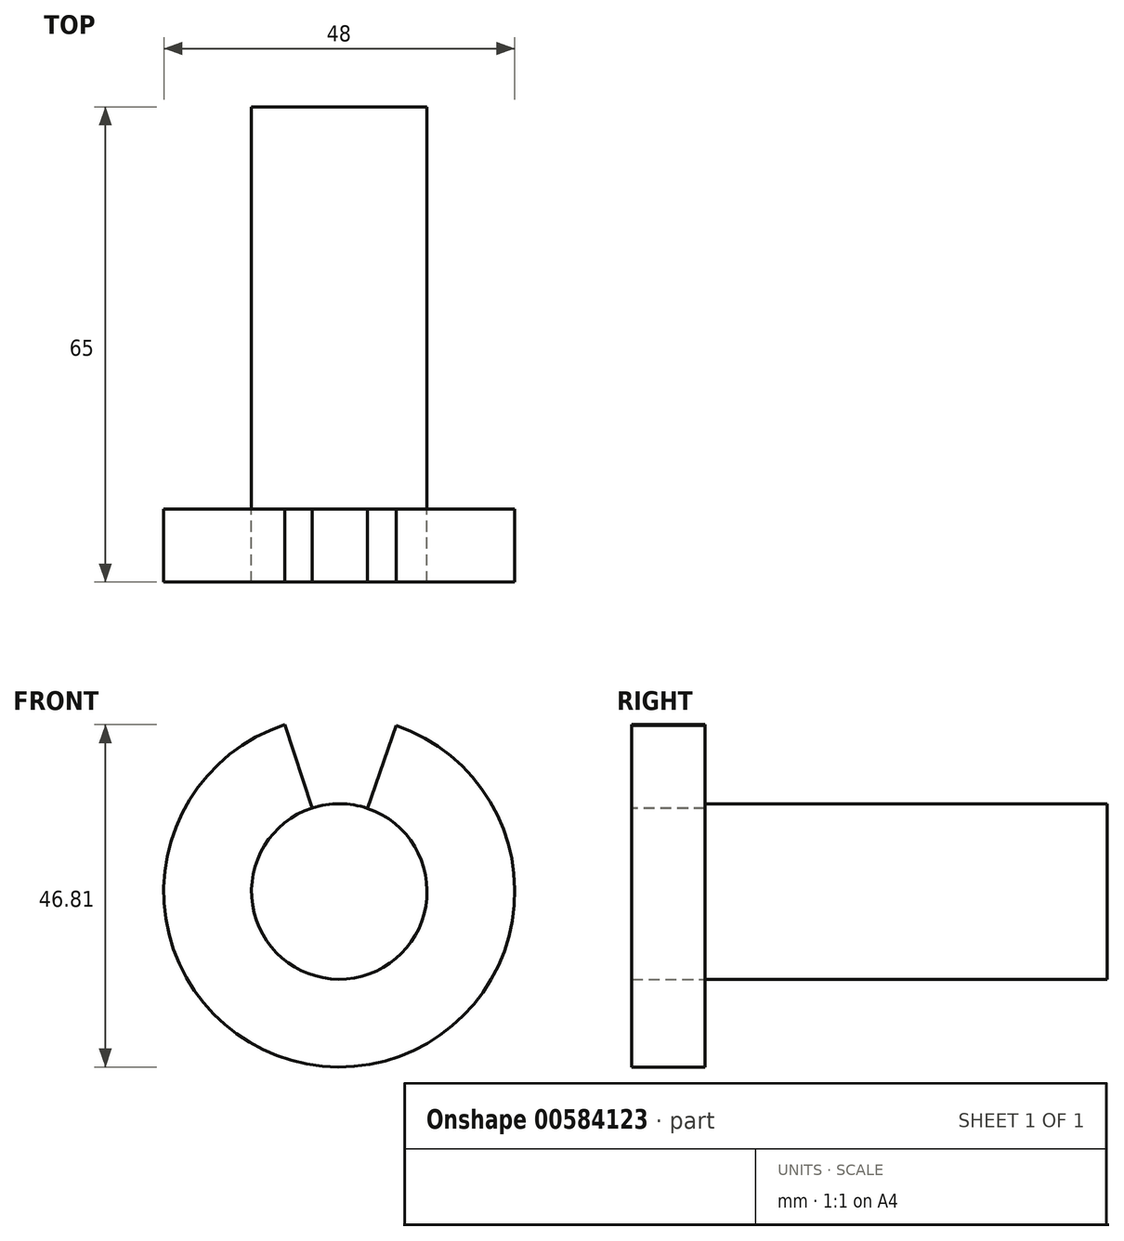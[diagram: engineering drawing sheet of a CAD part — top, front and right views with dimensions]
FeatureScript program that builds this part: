
annotation { "Feature Type Name" : "Feature", "Feature Type Description" : "" }
export const myFeature = defineFeature(function(context is Context, id is Id, definition is map)
    precondition{}
    {
        {
            var Q0;
            Q0=qCreatedBy(makeId("Front.planeOp"),FACE);
            var sketch = newSketch(context, id + "F0", { "sketchPlane" : qUnion([Q0])});
            skCircle(sketch, "E0", {"center": v(-28.82, 43.35) * mm, "radius": 12 * mm});
            skSolve(sketch);
        }
        {
            var Q0;
            Q0=makeQuery(id+"F0.imprint","IMPRINT",FACE,{"disambiguationData":[TD([[makeQuery(id+"F0.imprint","IMPRINT",EDGE,{"derivedFrom":sQuery(id+"F0.wireOp",EDGE,"E0")}),1.0]])]});
            var Q1;
            Q1=sQuery(id+"F0.wireOp",EDGE,"E0");
            extrude(context, id + "F1", {"entities" : qUnion([Q0]), "surfaceEntities" : qUnion([Q1]), "oppositeDirection" : true, "depth" : 55 * mm, "offsetDistance" : 25 * mm});
        }
        {
            var Q0;
            Q0=makeQuery(id+"F1.opExtrude","CAP_FACE",FACE,{"disambiguationData":[OSD([sQuery(id+"F0.wireOp",EDGE,"E0")])],"isStart":true});
            var sketch = newSketch(context, id + "F2", { "sketchPlane" : qUnion([Q0])});
            skCircle(sketch, "E1", {"center": v(-28.82, 43.35) * mm, "radius": 24 * mm});
            skSolve(sketch);
        }
        {
            var Q0;
            Q0=makeQuery(id+"F2.imprint","IMPRINT",FACE,{"disambiguationData":[TD([[makeQuery(id+"F2.imprint","IMPRINT",EDGE,{"derivedFrom":sQuery(id+"F2.wireOp",EDGE,"E1")}),1.0]])]});
            extrude(context, id + "F3", {"entities" : qUnion([Q0]), "depth" : 10 * mm, "offsetDistance" : 25 * mm});
        }
        {
            var Q0;
            Q0=makeQuery(id+"F3.opExtrude","CAP_FACE",FACE,{"disambiguationData":[OSD([sQuery(id+"F0.wireOp",EDGE,"E0"),sQuery(id+"F2.wireOp",EDGE,"E1")])],"isStart":false});
            var sketch = newSketch(context, id + "F4", { "sketchPlane" : qUnion([Q0])});
            skLineSegment(sketch, "E2", {"start": v(-28.82, 43.35) * mm, "end": v(-38.13, 71.77) * mm});
            skLineSegment(sketch, "E3", {"start": v(-28.82, 43.35) * mm, "end": v(-19.11, 71.77) * mm});
            skLineSegment(sketch, "E4", {"start": v(-19.11, 71.77) * mm, "end": v(-38.13, 71.77) * mm});
            skSolve(sketch);
        }
        {
            var Q0;
            {var subQ0=sQuery(id+"F4.wireOp",EDGE,"E2");var subQ1=makeQuery(id+"F3.opExtrude","CAP_EDGE",EDGE,{"disambiguationData":[OSD([sQuery(id+"F2.wireOp",EDGE,"E1")])],"isStart":false});var subQ2=makeQuery(id+"F4.imprint","INTERSECT",VERTEX,{"derivedFrom":[subQ1,subQ0]});Q0=makeQuery(id+"F4.imprint","IMPRINT",FACE,{"disambiguationData":[TD([[makeQuery(id+"F4.imprint","IMPRINT",EDGE,{"disambiguationData":[TD([[subQ2,1.0]])],"derivedFrom":subQ0}),-1.0]])]});}
            extrude(context, id + "F5", {"entities" : qUnion([Q0]), "operationType" : NewBodyOperationType.REMOVE, "oppositeDirection" : true, "depth" : 25 * mm, "offsetDistance" : 25 * mm});
        }
    });
